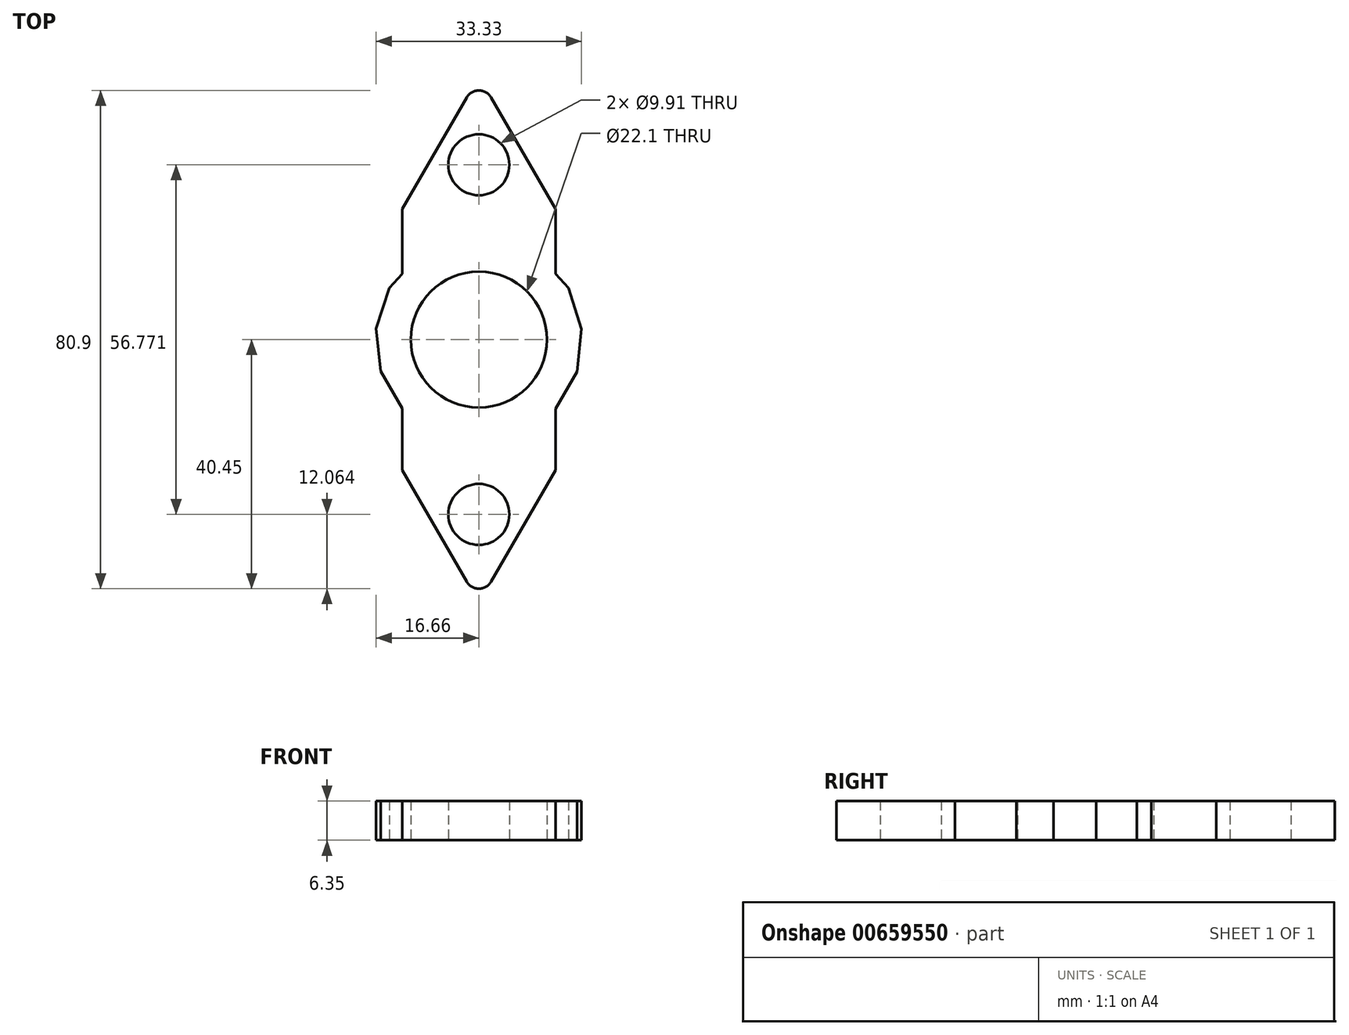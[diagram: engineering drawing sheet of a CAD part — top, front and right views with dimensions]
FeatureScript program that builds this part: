
annotation { "Feature Type Name" : "Feature", "Feature Type Description" : "" }
export const myFeature = defineFeature(function(context is Context, id is Id, definition is map)
    precondition{}
    {
        {
            var Q0;
            Q0=qCreatedBy(makeId("Top.planeOp"),FACE);
            var sketch = newSketch(context, id + "F0", { "sketchPlane" : qUnion([Q0])});
            skCircle(sketch, "E0", {"center": v(0, 0) * mm, "radius": 11.05 * mm});
            skCircle(sketch, "E1.cCircle", {"center": v(0, 28.39) * mm, "radius": 7.18 * mm, "construction": true});
            skLineSegment(sketch, "E1.0", {"start": v(1.98, 39.3) * mm, "end": v(12.43, 21.2) * mm});
            skLineSegment(sketch, "E1.2", {"start": v(-12.43, 21.2) * mm, "end": v(-1.98, 39.3) * mm});
            skPoint(sketch, "E1.0.midPoint", {"position": v(6.22, 31.97) * mm});
            skLineSegment(sketch, "E2", {"start": v(12.43, 21.2) * mm, "end": v(12.43, 10.69) * mm});
            skLineSegment(sketch, "E3", {"start": v(12.43, 10.69) * mm, "end": v(12.43, 21.2) * mm});
            skLineSegment(sketch, "E4", {"start": v(-12.43, 21.2) * mm, "end": v(-12.43, 10.69) * mm});
            skPoint(sketch, "E5.visualSharp", {"position": v(0, 42.74) * mm});
            skArc(sketch, "E5.filletArc", {"start": v(1.98, 39.3) * mm, "mid": v(0, 40.45) * mm, "end": v(-1.98, 39.3) * mm});
            skCircle(sketch, "E6", {"center": v(0, 28.39) * mm, "radius": 4.95 * mm});
            skLineSegment(sketch, "E7.1.0", {"start": v(-12.43, -10.69) * mm, "end": v(-12.43, -21.2) * mm});
            skLineSegment(sketch, "E7.1.1", {"start": v(-1.98, -39.3) * mm, "end": v(-12.43, -21.2) * mm});
            skArc(sketch, "E7.1.2", {"start": v(-1.98, -39.3) * mm, "mid": v(0, -40.45) * mm, "end": v(1.98, -39.3) * mm});
            skLineSegment(sketch, "E7.1.3", {"start": v(12.43, -21.2) * mm, "end": v(1.98, -39.3) * mm});
            skLineSegment(sketch, "E7.1.4", {"start": v(12.43, -21.2) * mm, "end": v(12.43, -10.69) * mm});
            skCircle(sketch, "E7.1.5", {"center": v(0, -28.39) * mm, "radius": 4.95 * mm});
            skArc(sketch, "E8.cCircle", {"start": v(-12.17, 10.98) * mm, "mid": v(-16.4, 0.2) * mm, "end": v(-12.43, -10.69) * mm, "construction": true});
            skLineSegment(sketch, "E8.0", {"start": v(15.93, -5.2) * mm, "end": v(12.44, -11.22) * mm});
            skLineSegment(sketch, "E8.1", {"start": v(12.44, -11.22) * mm, "end": v(12.43, -11.23) * mm});
            skLineSegment(sketch, "E8.4", {"start": v(-12.43, -11.23) * mm, "end": v(-12.46, -11.2) * mm});
            skLineSegment(sketch, "E8.5", {"start": v(-12.46, -11.2) * mm, "end": v(-15.94, -5.17) * mm});
            skLineSegment(sketch, "E8.6", {"start": v(-15.94, -5.17) * mm, "end": v(-16.66, 1.77) * mm});
            skLineSegment(sketch, "E8.7", {"start": v(-16.66, 1.77) * mm, "end": v(-14.5, 8.4) * mm});
            skLineSegment(sketch, "E8.8", {"start": v(-14.5, 8.4) * mm, "end": v(-12.17, 10.98) * mm});
            skLineSegment(sketch, "E8.12", {"start": v(12.2, 10.96) * mm, "end": v(14.52, 8.37) * mm});
            skLineSegment(sketch, "E8.13", {"start": v(14.52, 8.37) * mm, "end": v(16.67, 1.74) * mm});
            skLineSegment(sketch, "E8.14", {"start": v(16.67, 1.74) * mm, "end": v(15.93, -5.2) * mm});
            skPoint(sketch, "E8.0.midPoint", {"position": v(14.19, -8.2) * mm});
            skPoint(sketch, "E9.orphan", {"position": v(3.5, 16.39) * mm});
            skPoint(sketch, "E10.orphan", {"position": v(9.86, 13.55) * mm});
            skArc(sketch, "E11.trimOffspring", {"start": v(12.43, -10.69) * mm, "mid": v(16.4, 0.18) * mm, "end": v(12.2, 10.96) * mm, "construction": true});
            skPoint(sketch, "E12.orphan", {"position": v(-6.83, -15.3) * mm});
            skPoint(sketch, "E13.orphan", {"position": v(-9.84, 13.57) * mm});
            skPoint(sketch, "E14.orphan", {"position": v(-12.43, 0) * mm});
            skPoint(sketch, "E15.orphan", {"position": v(12.43, 0) * mm});
            skSolve(sketch);
        }
        {
            var Q0;
            Q0=makeQuery(id+"F0.imprint","IMPRINT",FACE,{"disambiguationData":[TD([[makeQuery(id+"F0.imprint","IMPRINT",EDGE,{"derivedFrom":sQuery(id+"F0.wireOp",EDGE,"E0")}),-1.0]])]});
            extrude(context, id + "F1", {"entities" : qUnion([Q0]), "depth" : 6.35 * mm, "offsetDistance" : 25.4 * mm});
        }
    });
